# Revit family: Metal_Lockers-Salsbury_Industries-S_65000_66000_Series-1_Wide_Units
name_source: partatom
category: Specialty Equipment
revit_build: Autodesk Revit 2016 (Build: 20150714_1515(x64)
units: mm (PartAtom-declared; Revit-internal decimal feet)

## family parameters
Always vertical = Yes
Cut with Voids When Loaded = No
OmniClass Number = 23.40.00.00
OmniClass Title = Equipment and Furnishings
Part Type = Normal
Room Calculation Point = No
Round Connector Dimension = Use Diameter
Shared = No
Work Plane-Based = No

## types (18) — shared parameters
Assembly Code = C1030310
Door Window Height = 7 "
Door Window Width = 6 "
Hasp Handle Material = Plastic - Salsbury Finish - Black
Hasp Plate Rivet Material = Steel -Salsbury Finish - Polished Steel
Manufacturer = Salsbury Industries
MasterFormat Number = 10 51 13
MasterFormat Title = Lockers
OmniClass 23 Number = 23.40.00.00
OmniClass 23 Title = Equipment and Furnishings
URL = www.lockers.com
Version = 3.0 (03/30/18)
Width = 12.04 "
Window Panel Material = Polycarbonate - Salsbury Finish - Clear

## per-type parameters (varying)
| type | Base Height | Compartment Divider Height | Depth | Description | Door Location D1 | Door Window Offset | Individual Door Height | Model | Sloping Hood Height | Standard Leg Base | Top Compartment Divider | Top Door | Type Comments | Unit Height | Zee Base |
| S-66162 - with Standard 6" High Legs | 6 " | 11.159 " | 12.01 " | 1 Wide - 6 Feet High - 12 Inches Deep | See-Through Metal Locker Doors-12 inch with Latch Hasps : Six Tier Door - 6 foot | 3.372 " | 11.534 " | S-66162 | 6.625 " | Metal Locker Legs : 6" High - 12" W x 12" D | Yes | Yes | See-Through Metal Locker - Six Tier | 72 " | Metal Locker Zee Base : None |
| S-66165 - with Standard 6" High Legs | 6 " | 11.159 " | 15.01 " | 1 Wide - 6 Feet High - 15 Inches Deep | See-Through Metal Locker Doors-12 inch with Latch Hasps : Six Tier Door - 6 foot | 3.372 " | 11.534 " | S-66165 | 8.682 " | Metal Locker Legs : 6" High - 12" W x 15" D | Yes | Yes | See-Through Metal Locker - Six Tier | 72 " | Metal Locker Zee Base : None |
| S-66168 - with Standard 6" High Legs | 6 " | 11.159 " | 18.01 " | 1 Wide - 6 Feet High - 18 Inches Deep | See-Through Metal Locker Doors-12 inch with Latch Hasps : Six Tier Door - 6 foot | 3.372 " | 11.534 " | S-66168 | 10.739 " | Metal Locker Legs : 6" High - 12"W x 18"D | Yes | Yes | See-Through Metal Locker - Six Tier | 72 " | Metal Locker Zee Base : None |
| S-66162 - with 77572 Zee Base and 77550 Lockers without Legs | 4 " | 11.159 " | 12.01 " | 1 Wide - 6 Feet High - 12 Inches Deep with Zee Base and Lockers without Legs | See-Through Metal Locker Doors-12 inch with Latch Hasps : Six Tier Door - 6 foot | 3.372 " | 11.534 " | S-66162 with 77572 and 77550 | 6.625 " | Metal Locker Legs : No Legs | Yes | Yes | See-Through Metal Locker - Six Tier | 72 " | Metal Locker Zee Base : 77572- 12" W x 12" D |
| S-66165 - with 77575 Zee Base and 77550 Lockers without Legs | 4 " | 11.159 " | 15.01 " | 1 Wide - 6 Feet High - 15 Inches Deep with Zee Base and Lockers without Legs | See-Through Metal Locker Doors-12 inch with Latch Hasps : Six Tier Door - 6 foot | 3.372 " | 11.534 " | S-66165 with 77575 and 77550 | 8.682 " | Metal Locker Legs : No Legs | Yes | Yes | See-Through Metal Locker - Six Tier | 72 " | Metal Locker Zee Base : 77575 - 12" W x 15" D |
| S-66168 - with 77578 Zee Base and 77550 Lockers without Legs | 4 " | 11.159 " | 18.01 " | 1 Wide - 6 Feet High - 18 Inches Deep with Zee Base and Lockers without Legs | See-Through Metal Locker Doors-12 inch with Latch Hasps : Six Tier Door - 6 foot | 3.372 " | 11.534 " | S-66168 with 77578 and 77550 | 10.739 " | Metal Locker Legs : No Legs | Yes | Yes | See-Through Metal Locker - Six Tier | 72 " | Metal Locker Zee Base : 77578 - 12"W x 18"D |
| S-66162 - with 77550 Lockers without Legs | 0 " | 11.159 " | 12.01 " | 1 Wide - 6 Feet High - 12 Inches Deep with Lockers without Legs | See-Through Metal Locker Doors-12 inch with Latch Hasps : Six Tier Door - 6 foot | 3.372 " | 11.534 " | S-66162 with 77550 | 6.625 " | Metal Locker Legs : No Legs | Yes | Yes | See-Through Metal Locker - Six Tier | 72 " | Metal Locker Zee Base : None |
| S-66165 - with 77550 Lockers without Legs | 0 " | 11.159 " | 15.01 " | 1 Wide - 6 Feet High - 15 Inches Deep with Lockers without Legs | See-Through Metal Locker Doors-12 inch with Latch Hasps : Six Tier Door - 6 foot | 3.372 " | 11.534 " | S-66165 with 77550 | 8.682 " | Metal Locker Legs : No Legs | Yes | Yes | See-Through Metal Locker - Six Tier | 72 " | Metal Locker Zee Base : None |
| S-66168 - with 77550 Lockers without Legs | 0 " | 11.159 " | 18.01 " | 1 Wide - 6 Feet High - 18 Inches Deep with Lockers without Legs | See-Through Metal Locker Doors-12 inch with Latch Hasps : Six Tier Door - 6 foot | 3.372 " | 11.534 " | S-66168 with 77550 | 10.739 " | Metal Locker Legs : No Legs | Yes | Yes | See-Through Metal Locker - Six Tier | 72 " | Metal Locker Zee Base : None |
| S-65152 - with Standard 6" High Legs | 6 " | 11.088 " | 12.01 " | 1 Wide - 5 Feet High - 12 Inches Deep | See-Through Metal Locker Doors-12 inch with Latch Hasps : Five Tier Door - 5 foot | 3.303 " | 11.463 " | S-65152 | 6.625 " | Metal Locker Legs : 6" High - 12" W x 12" D | No | No | See-Through Metal Locker - Five Tier | 60 " | Metal Locker Zee Base : None |
| S-65152 - with 77572 Zee Base and 77550 Lockers without Legs | 4 " | 11.088 " | 12.01 " | 1 Wide - 5 Feet High - 12 Inches Deep with Zee Base and Lockers without Legs | See-Through Metal Locker Doors-12 inch with Latch Hasps : Five Tier Door - 5 foot | 3.303 " | 11.463 " | S-65152 with 77572 and 77550 | 6.625 " | Metal Locker Legs : No Legs | No | No | See-Through Metal Locker - Five Tier | 60 " | Metal Locker Zee Base : 77572- 12" W x 12" D |
| S-65152 - with 77550 Lockers without Legs | 0 " | 11.088 " | 12.01 " | 1 Wide - 5 Feet High - 12 Inches Deep with Lockers without Legs | See-Through Metal Locker Doors-12 inch with Latch Hasps : Five Tier Door - 5 foot | 3.303 " | 11.463 " | S-65152 with 77550 | 6.625 " | Metal Locker Legs : No Legs | No | No | See-Through Metal Locker - Five Tier | 60 " | Metal Locker Zee Base : None |
| S-65155 - with Standard 6" High Legs | 6 " | 11.088 " | 15.01 " | 1 Wide - 5 Feet High - 15 Inches Deep | See-Through Metal Locker Doors-12 inch with Latch Hasps : Five Tier Door - 5 foot | 3.303 " | 11.463 " | S-65155 | 8.682 " | Metal Locker Legs : 6" High - 12" W x 15" D | No | No | See-Through Metal Locker - Five Tier | 60 " | Metal Locker Zee Base : None |
| S-65155 - with 77575 Zee Base and 77550 Lockers without Legs | 4 " | 11.088 " | 15.01 " | 1 Wide - 5 Feet High - 15 Inches Deep with Zee Base and Lockers without Legs | See-Through Metal Locker Doors-12 inch with Latch Hasps : Five Tier Door - 5 foot | 3.303 " | 11.463 " | S-65155 with 77575 and 77550 | 8.682 " | Metal Locker Legs : No Legs | No | No | See-Through Metal Locker - Five Tier | 60 " | Metal Locker Zee Base : 77575 - 12" W x 15" D |
| S-65155 - with 77550 Lockers without Legs | 0 " | 11.088 " | 15.01 " | 1 Wide - 5 Feet High - 15 Inches Deep with Lockers without Legs | See-Through Metal Locker Doors-12 inch with Latch Hasps : Five Tier Door - 5 foot | 3.303 " | 11.463 " | S-65165 with 77550 | 8.682 " | Metal Locker Legs : No Legs | No | No | See-Through Metal Locker - Five Tier | 60 " | Metal Locker Zee Base : None |
| S-65158 - with Standard 6" High Legs | 6 " | 11.088 " | 18.01 " | 1 Wide - 5 Feet High - 18 Inches Deep | See-Through Metal Locker Doors-12 inch with Latch Hasps : Five Tier Door - 5 foot | 3.303 " | 11.463 " | S-65158 | 10.739 " | Metal Locker Legs : 6" High - 12"W x 18"D | No | No | See-Through Metal Locker - Five Tier | 60 " | Metal Locker Zee Base : None |
| S-65158 - with 77578 Zee Base and 77550 Lockers without Legs | 4 " | 11.088 " | 18.01 " | 1 Wide - 5 Feet High - 18 Inches Deep with Zee Base and Lockers without Legs | See-Through Metal Locker Doors-12 inch with Latch Hasps : Five Tier Door - 5 foot | 3.303 " | 11.463 " | S-65158 with 77578 and 77550 | 10.739 " | Metal Locker Legs : No Legs | No | No | See-Through Metal Locker - Five Tier | 60 " | Metal Locker Zee Base : 77578 - 12"W x 18"D |
| S-65158 - with 77550 Lockers without Legs | 0 " | 11.088 " | 18.01 " | 1 Wide - 5 Feet High - 18 Inches Deep with Lockers without Legs | See-Through Metal Locker Doors-12 inch with Latch Hasps : Five Tier Door - 5 foot | 3.303 " | 11.463 " | S-65158 with 77550 | 10.739 " | Metal Locker Legs : No Legs | No | No | See-Through Metal Locker - Five Tier | 60 " | Metal Locker Zee Base : None |

## geometry (parser evidence)
native form markers: Sweep x46
no freeform markers — native parametric forms only
